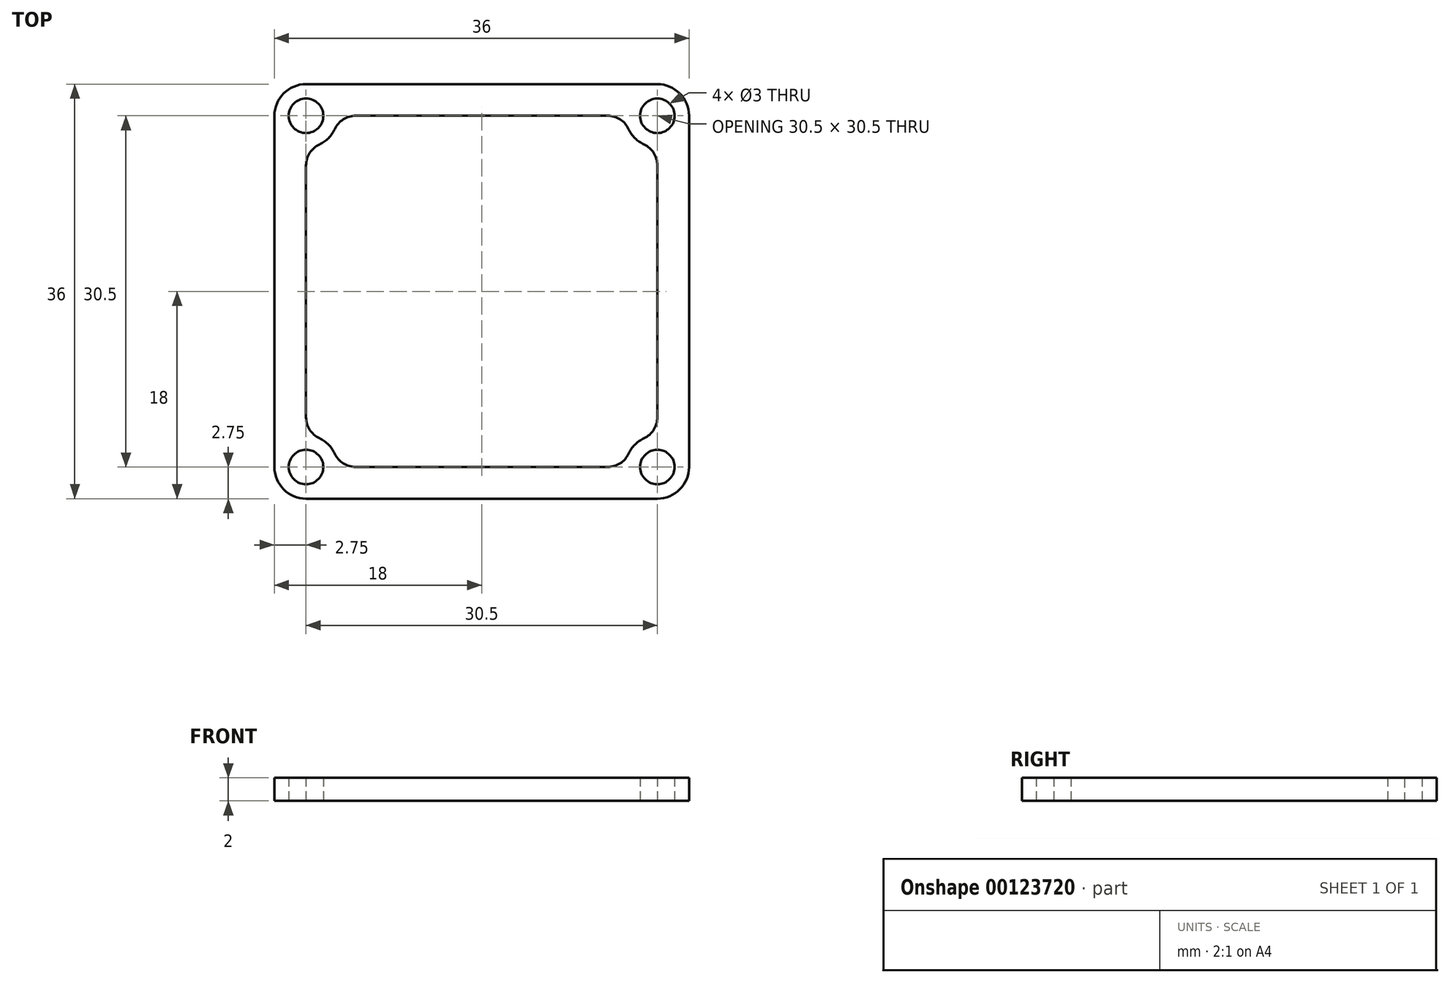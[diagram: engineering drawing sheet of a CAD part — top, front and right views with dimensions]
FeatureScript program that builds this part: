
annotation { "Feature Type Name" : "Feature", "Feature Type Description" : "" }
export const myFeature = defineFeature(function(context is Context, id is Id, definition is map)
    precondition{}
    {
        {
            var Q0;
            Q0=qCreatedBy(makeId("Top.planeOp"),FACE);
            var sketch = newSketch(context, id + "F0", { "sketchPlane" : qUnion([Q0])});
            skLineSegment(sketch, "E0.bottom", {"start": v(-15.25, 18) * mm, "end": v(15.25, 18) * mm});
            skLineSegment(sketch, "E0.top", {"start": v(-15.25, -18) * mm, "end": v(15.25, -18) * mm});
            skLineSegment(sketch, "E0.left", {"start": v(-18, 15.25) * mm, "end": v(-18, -15.25) * mm});
            skLineSegment(sketch, "E0.right", {"start": v(18, 15.25) * mm, "end": v(18, -15.25) * mm});
            skPoint(sketch, "E1.visualSharp", {"position": v(-18, 18) * mm});
            skArc(sketch, "E1.filletArc", {"start": v(-15.25, 18) * mm, "mid": v(-17.2, 17.2) * mm, "end": v(-18, 15.25) * mm});
            skPoint(sketch, "E2.visualSharp", {"position": v(-18, -18) * mm});
            skArc(sketch, "E2.filletArc", {"start": v(-18, -15.25) * mm, "mid": v(-17.2, -17.2) * mm, "end": v(-15.25, -18) * mm});
            skPoint(sketch, "E3.visualSharp", {"position": v(18, -18) * mm});
            skArc(sketch, "E3.filletArc", {"start": v(15.25, -18) * mm, "mid": v(17.2, -17.2) * mm, "end": v(18, -15.25) * mm});
            skPoint(sketch, "E4.visualSharp", {"position": v(18, 18) * mm});
            skArc(sketch, "E4.filletArc", {"start": v(18, 15.25) * mm, "mid": v(17.2, 17.2) * mm, "end": v(15.25, 18) * mm});
            skCircle(sketch, "E5", {"center": v(-15.25, -15.25) * mm, "radius": 1.5 * mm});
            skCircle(sketch, "E6.0.1.0", {"center": v(-15.25, 15.25) * mm, "radius": 1.5 * mm});
            skCircle(sketch, "E6.1.0.0", {"center": v(15.25, -15.25) * mm, "radius": 1.5 * mm});
            skCircle(sketch, "E6.1.1.0", {"center": v(15.25, 15.25) * mm, "radius": 1.5 * mm});
            skLineSegment(sketch, "E6.direction1", {"start": v(-15.25, -15.25) * mm, "end": v(15.25, -15.25) * mm, "construction": true});
            skLineSegment(sketch, "E6.direction2", {"start": v(-15.25, -15.25) * mm, "end": v(-15.25, 15.25) * mm, "construction": true});
            skLineSegment(sketch, "E7", {"start": v(-15.25, 12.5) * mm, "end": v(-15.25, -12.5) * mm});
            skLineSegment(sketch, "E8", {"start": v(-12.5, -15.25) * mm, "end": v(12.5, -15.25) * mm});
            skLineSegment(sketch, "E9", {"start": v(15.25, -12.5) * mm, "end": v(15.25, 12.5) * mm});
            skLineSegment(sketch, "E10", {"start": v(-12.5, 15.25) * mm, "end": v(12.5, 15.25) * mm});
            skArc(sketch, "E11", {"start": v(-12.5, -15.25) * mm, "mid": v(-13.3, -13.3) * mm, "end": v(-15.25, -12.5) * mm});
            skArc(sketch, "E12", {"start": v(-15.25, 12.5) * mm, "mid": v(-13.3, 13.3) * mm, "end": v(-12.5, 15.25) * mm});
            skArc(sketch, "E13", {"start": v(12.5, 15.25) * mm, "mid": v(13.3, 13.3) * mm, "end": v(15.25, 12.5) * mm});
            skArc(sketch, "E14", {"start": v(15.25, -12.5) * mm, "mid": v(13.3, -13.3) * mm, "end": v(12.5, -15.25) * mm});
            skSolve(sketch);
        }
        {
            var Q0;
            Q0 = qSketchRegion(id + "F0", true);
            extrude(context, id + "F1", {"entities" : qUnion([Q0]), "depth" : 2 * mm});
        }
        {
            var Q0;
            Q0=makeQuery(id+"F1.opExtrude","SWEPT_EDGE",EDGE,{"disambiguationData":[OSD([sQuery(id+"F0.wireOp",EDGE,"E7"),sQuery(id+"F0.wireOp",EDGE,"E12")])]});
            var Q1;
            Q1=makeQuery(id+"F1.opExtrude","SWEPT_EDGE",EDGE,{"disambiguationData":[OSD([sQuery(id+"F0.wireOp",EDGE,"E10"),sQuery(id+"F0.wireOp",EDGE,"E12")])]});
            var Q2;
            Q2=makeQuery(id+"F1.opExtrude","SWEPT_EDGE",EDGE,{"disambiguationData":[OSD([sQuery(id+"F0.wireOp",EDGE,"E10"),sQuery(id+"F0.wireOp",EDGE,"E13")])]});
            var Q3;
            Q3=makeQuery(id+"F1.opExtrude","SWEPT_EDGE",EDGE,{"disambiguationData":[OSD([sQuery(id+"F0.wireOp",EDGE,"E9"),sQuery(id+"F0.wireOp",EDGE,"E13")])]});
            var Q4;
            Q4=makeQuery(id+"F1.opExtrude","SWEPT_EDGE",EDGE,{"disambiguationData":[OSD([sQuery(id+"F0.wireOp",EDGE,"E9"),sQuery(id+"F0.wireOp",EDGE,"E14")])]});
            var Q5;
            Q5=makeQuery(id+"F1.opExtrude","SWEPT_EDGE",EDGE,{"disambiguationData":[OSD([sQuery(id+"F0.wireOp",EDGE,"E8"),sQuery(id+"F0.wireOp",EDGE,"E14")])]});
            var Q6;
            Q6=makeQuery(id+"F1.opExtrude","SWEPT_EDGE",EDGE,{"disambiguationData":[OSD([sQuery(id+"F0.wireOp",EDGE,"E7"),sQuery(id+"F0.wireOp",EDGE,"E11")])]});
            var Q7;
            Q7=makeQuery(id+"F1.opExtrude","SWEPT_EDGE",EDGE,{"disambiguationData":[OSD([sQuery(id+"F0.wireOp",EDGE,"E8"),sQuery(id+"F0.wireOp",EDGE,"E11")])]});
            fillet(context, id + "F2", {"entities" : qUnion([Q0, Q1, Q2, Q3, Q4, Q5, Q6, Q7]), "radius" : 2 * mm, "tangentPropagation" : true, "allowEdgeOverflow" : false});
        }
    });
